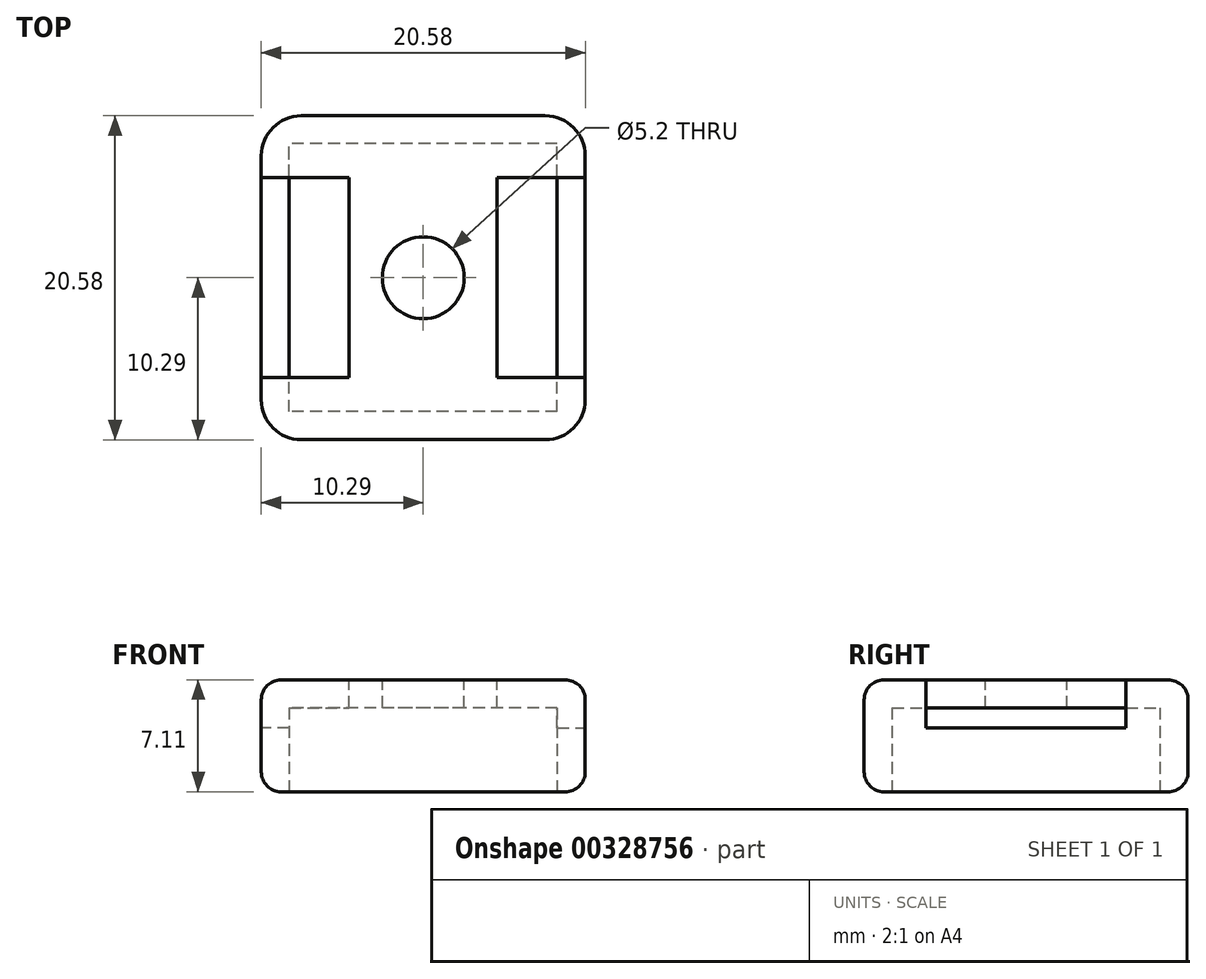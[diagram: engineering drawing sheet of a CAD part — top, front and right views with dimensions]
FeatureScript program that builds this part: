
annotation { "Feature Type Name" : "Feature", "Feature Type Description" : "" }
export const myFeature = defineFeature(function(context is Context, id is Id, definition is map)
    precondition{}
    {
        {
            var Q0;
            Q0=qCreatedBy(makeId("Top.planeOp"),FACE);
            var sketch = newSketch(context, id + "F0", { "sketchPlane" : qUnion([Q0])});
            skLineSegment(sketch, "E0.bottom", {"start": v(10.29, 10.29) * mm, "end": v(-10.29, 10.29) * mm});
            skLineSegment(sketch, "E0.top", {"start": v(10.29, -10.29) * mm, "end": v(-10.29, -10.29) * mm});
            skLineSegment(sketch, "E0.left", {"start": v(10.29, 10.29) * mm, "end": v(10.29, -10.29) * mm});
            skLineSegment(sketch, "E0.right", {"start": v(-10.29, 10.29) * mm, "end": v(-10.29, -10.29) * mm});
            skPoint(sketch, "E0.middle", {"position": v(0, 0) * mm});
            skSolve(sketch);
        }
        {
            var Q0;
            Q0 = qSketchRegion(id + "F0", true);
            extrude(context, id + "F1", {"entities" : qUnion([Q0]), "depth" : 7.11 * mm});
        }
        {
            var Q0;
            Q0=makeQuery(id+"F1.opExtrude","CAP_FACE",FACE,{"disambiguationData":[OSD([sQuery(id+"F0.wireOp",EDGE,"E0.bottom"),sQuery(id+"F0.wireOp",EDGE,"E0.top"),sQuery(id+"F0.wireOp",EDGE,"E0.left"),sQuery(id+"F0.wireOp",EDGE,"E0.right")])],"isStart":true});
            var sketch = newSketch(context, id + "F2", { "sketchPlane" : qUnion([Q0])});
            skLineSegment(sketch, "E1.bottom", {"start": v(8.5, 8.5) * mm, "end": v(-8.5, 8.5) * mm});
            skLineSegment(sketch, "E1.top", {"start": v(8.5, -8.5) * mm, "end": v(-8.5, -8.5) * mm});
            skLineSegment(sketch, "E1.left", {"start": v(8.5, 8.5) * mm, "end": v(8.5, -8.5) * mm});
            skLineSegment(sketch, "E1.right", {"start": v(-8.5, 8.5) * mm, "end": v(-8.5, -8.5) * mm});
            skPoint(sketch, "E1.middle", {"position": v(0, 0) * mm});
            skSolve(sketch);
        }
        {
            var Q0;
            Q0=makeQuery(id+"F2.imprint","IMPRINT",FACE,{"disambiguationData":[TD([[makeQuery(id+"F2.imprint","IMPRINT",EDGE,{"derivedFrom":sQuery(id+"F2.wireOp",EDGE,"E1.bottom")}),1.0]])]});
            extrude(context, id + "F3", {"entities" : qUnion([Q0]), "operationType" : NewBodyOperationType.REMOVE, "oppositeDirection" : true, "depth" : 5.33 * mm});
        }
        {
            var Q0;
            Q0=makeQuery(id+"F1.opExtrude","SWEPT_EDGE",EDGE,{"disambiguationData":[OSD([sQuery(id+"F0.wireOp",EDGE,"E0.top"),sQuery(id+"F0.wireOp",EDGE,"E0.right")])]});
            var Q1;
            Q1=makeQuery(id+"F1.opExtrude","SWEPT_EDGE",EDGE,{"disambiguationData":[OSD([sQuery(id+"F0.wireOp",EDGE,"E0.bottom"),sQuery(id+"F0.wireOp",EDGE,"E0.left")])]});
            var Q2;
            Q2=makeQuery(id+"F1.opExtrude","SWEPT_EDGE",EDGE,{"disambiguationData":[OSD([sQuery(id+"F0.wireOp",EDGE,"E0.top"),sQuery(id+"F0.wireOp",EDGE,"E0.left")])]});
            var Q3;
            Q3=makeQuery(id+"F1.opExtrude","SWEPT_EDGE",EDGE,{"disambiguationData":[OSD([sQuery(id+"F0.wireOp",EDGE,"E0.bottom"),sQuery(id+"F0.wireOp",EDGE,"E0.right")])]});
            fillet(context, id + "F4", {"entities" : qUnion([Q0, Q1, Q2, Q3]), "radius" : 2.54 * mm, "tangentPropagation" : true, "allowEdgeOverflow" : false});
        }
        {
            var Q0;
            Q0=makeQuery(id+"F1.opExtrude","CAP_FACE",FACE,{"disambiguationData":[OSD([sQuery(id+"F0.wireOp",EDGE,"E0.bottom"),sQuery(id+"F0.wireOp",EDGE,"E0.top"),sQuery(id+"F0.wireOp",EDGE,"E0.left"),sQuery(id+"F0.wireOp",EDGE,"E0.right")])],"isStart":false});
            var sketch = newSketch(context, id + "F5", { "sketchPlane" : qUnion([Q0])});
            skLineSegment(sketch, "E2.bottom", {"start": v(-4.7, 6.35) * mm, "end": v(-15.88, 6.35) * mm});
            skLineSegment(sketch, "E2.top", {"start": v(-4.7, -6.35) * mm, "end": v(-15.88, -6.35) * mm});
            skLineSegment(sketch, "E2.left", {"start": v(-4.7, 6.35) * mm, "end": v(-4.7, -6.35) * mm});
            skLineSegment(sketch, "E2.right", {"start": v(-15.88, 6.35) * mm, "end": v(-15.88, -6.35) * mm});
            skPoint(sketch, "E2.middle", {"position": v(-10.29, 0) * mm});
            skSolve(sketch);
        }
        {
            var Q0;
            {var subQ0=sQuery(id+"F5.wireOp",EDGE,"E2.left");Q0=makeQuery(id+"F5.imprint","IMPRINT",FACE,{"disambiguationData":[TD([[makeQuery(id+"F5.imprint","IMPRINT",EDGE,{"derivedFrom":subQ0}),-1.0]])]});}
            extrude(context, id + "F6", {"entities" : qUnion([Q0]), "operationType" : NewBodyOperationType.REMOVE, "oppositeDirection" : true, "depth" : 3.05 * mm});
        }
        {
            var Q0;
            Q0=makeQuery(id+"F1.opExtrude","CAP_FACE",FACE,{"disambiguationData":[OSD([sQuery(id+"F0.wireOp",EDGE,"E0.bottom"),sQuery(id+"F0.wireOp",EDGE,"E0.top"),sQuery(id+"F0.wireOp",EDGE,"E0.left"),sQuery(id+"F0.wireOp",EDGE,"E0.right")])],"isStart":false});
            var sketch = newSketch(context, id + "F7", { "sketchPlane" : qUnion([Q0])});
            skLineSegment(sketch, "E3.bottom", {"start": v(4.7, 6.35) * mm, "end": v(15.88, 6.35) * mm});
            skLineSegment(sketch, "E3.top", {"start": v(4.7, -6.35) * mm, "end": v(15.88, -6.35) * mm});
            skLineSegment(sketch, "E3.left", {"start": v(4.7, 6.35) * mm, "end": v(4.7, -6.35) * mm});
            skLineSegment(sketch, "E3.right", {"start": v(15.88, 6.35) * mm, "end": v(15.88, -6.35) * mm});
            skPoint(sketch, "E3.middle", {"position": v(10.29, 0) * mm});
            skSolve(sketch);
        }
        {
            var Q0;
            Q0 = qSketchRegion(id + "F7", true);
            extrude(context, id + "F8", {"entities" : qUnion([Q0]), "operationType" : NewBodyOperationType.REMOVE, "oppositeDirection" : true, "depth" : 3.05 * mm});
        }
        {
            var Q0;
            Q0=makeQuery(id+"F1.opExtrude","CAP_FACE",FACE,{"disambiguationData":[OSD([sQuery(id+"F0.wireOp",EDGE,"E0.bottom"),sQuery(id+"F0.wireOp",EDGE,"E0.top"),sQuery(id+"F0.wireOp",EDGE,"E0.left"),sQuery(id+"F0.wireOp",EDGE,"E0.right")])],"isStart":false});
            var sketch = newSketch(context, id + "F9", { "sketchPlane" : qUnion([Q0])});
            skCircle(sketch, "E4", {"center": v(0, 0) * mm, "radius": 2.6 * mm});
            skSolve(sketch);
        }
        {
            var Q0;
            Q0 = qSketchRegion(id + "F9", true);
            extrude(context, id + "F10", {"entities" : qUnion([Q0]), "operationType" : NewBodyOperationType.REMOVE, "oppositeDirection" : true, "depth" : 1.78 * mm});
        }
        {
            var Q0;
            Q0=makeQuery(id+"F1.opExtrude","CAP_EDGE",EDGE,{"disambiguationData":[OSD([sQuery(id+"F0.wireOp",EDGE,"E0.bottom")])],"isStart":false});
            var Q1;
            Q1=makeQuery(id+"F1.opExtrude","CAP_EDGE",EDGE,{"disambiguationData":[OSD([sQuery(id+"F0.wireOp",EDGE,"E0.top")])],"isStart":false});
            fillet(context, id + "F11", {"entities" : qUnion([Q0, Q1]), "radius" : 1.27 * mm, "tangentPropagation" : true, "allowEdgeOverflow" : false});
        }
        {
            var Q0;
            Q0=makeQuery(id+"F1.opExtrude","CAP_EDGE",EDGE,{"disambiguationData":[OSD([sQuery(id+"F0.wireOp",EDGE,"E0.right")])],"isStart":true});
            var Q1;
            Q1=makeQuery(id+"F1.opExtrude","CAP_EDGE",EDGE,{"disambiguationData":[OSD([sQuery(id+"F0.wireOp",EDGE,"E0.bottom")])],"isStart":true});
            var Q2;
            {var subQ0=sQuery(id+"F0.wireOp",EDGE,"E0.right");var subQ1=sQuery(id+"F0.wireOp",EDGE,"E0.bottom");Q2=makeQuery(id+"F4.opFillet","BLEND_EDGE",EDGE,{"blendedFrom":[makeQuery(id+"F1.opExtrude","SWEPT_EDGE",EDGE,{"disambiguationData":[OSD([subQ1,subQ0])]}),makeQuery(id+"F1.opExtrude","CAP_FACE",FACE,{"disambiguationData":[OSD([subQ1,sQuery(id+"F0.wireOp",EDGE,"E0.top"),sQuery(id+"F0.wireOp",EDGE,"E0.left"),subQ0])],"isStart":true})],"blendedInto":[makeQuery(id+"F1.opExtrude","CAP_FACE",FACE,{"disambiguationData":[OSD([subQ1,sQuery(id+"F0.wireOp",EDGE,"E0.top"),sQuery(id+"F0.wireOp",EDGE,"E0.left"),subQ0])],"isStart":true})]});}
            fillet(context, id + "F12", {"entities" : qUnion([Q0, Q1, Q2]), "radius" : 1.27 * mm, "tangentPropagation" : true, "allowEdgeOverflow" : false});
        }
    });
